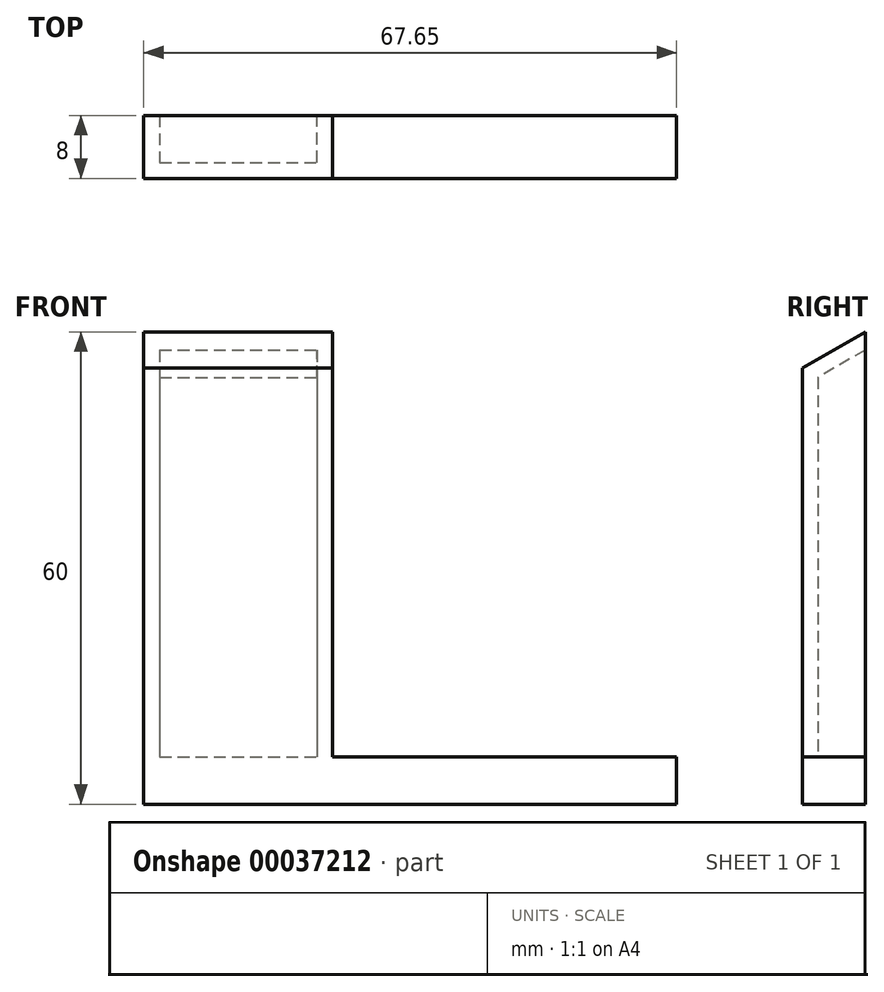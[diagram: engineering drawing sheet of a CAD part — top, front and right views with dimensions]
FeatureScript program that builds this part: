
annotation { "Feature Type Name" : "Feature", "Feature Type Description" : "" }
export const myFeature = defineFeature(function(context is Context, id is Id, definition is map)
    precondition{}
    {
        {
            var Q0;
            Q0=qCreatedBy(makeId("Front.planeOp"),FACE);
            var sketch = newSketch(context, id + "F0", { "sketchPlane" : qUnion([Q0])});
            skLineSegment(sketch, "E0.rect.bottom", {"start": v(-12, 27) * mm, "end": v(12, 27) * mm, "construction": true});
            skLineSegment(sketch, "E0.rect.top", {"start": v(-12, -27) * mm, "end": v(12, -27) * mm, "construction": true});
            skLineSegment(sketch, "E0.rect.left", {"start": v(-12, 27) * mm, "end": v(-12, -27) * mm, "construction": true});
            skLineSegment(sketch, "E0.rect.right", {"start": v(12, 27) * mm, "end": v(12, -27) * mm, "construction": true});
            skPoint(sketch, "E0.rect.middle", {"position": v(0, 0) * mm});
            skLineSegment(sketch, "E1.rect.bottom", {"start": v(-12, 27) * mm, "end": v(12, 27) * mm});
            skLineSegment(sketch, "E1.rect.top", {"start": v(-12, -27) * mm, "end": v(12, -27) * mm});
            skLineSegment(sketch, "E1.rect.left", {"start": v(-12, 27) * mm, "end": v(-12, -27) * mm});
            skLineSegment(sketch, "E1.rect.right", {"start": v(12, 27) * mm, "end": v(12, -27) * mm});
            skLineSegment(sketch, "E2.rect.bottom", {"start": v(-10, 25) * mm, "end": v(10, 25) * mm});
            skLineSegment(sketch, "E2.rect.top", {"start": v(-10, -25) * mm, "end": v(10, -25) * mm});
            skLineSegment(sketch, "E2.rect.left", {"start": v(-10, 25) * mm, "end": v(-10, -25) * mm});
            skLineSegment(sketch, "E2.rect.right", {"start": v(10, 25) * mm, "end": v(10, -25) * mm});
            skLineSegment(sketch, "E3", {"start": v(-10, -25) * mm, "end": v(-10, -27) * mm});
            skLineSegment(sketch, "E4", {"start": v(10, -25) * mm, "end": v(10, -27) * mm});
            skSolve(sketch);
        }
        {
            var Q0;
            Q0=makeQuery(id+"F0.imprint","IMPRINT",FACE,{"disambiguationData":[TD([[makeQuery(id+"F0.imprint","IMPRINT",EDGE,{"derivedFrom":sQuery(id+"F0.wireOp",EDGE,"E1.rect.bottom")}),-1.0]])]});
            var Q1;
            Q1=makeQuery(id+"F0.imprint","IMPRINT",FACE,{"disambiguationData":[TD([[makeQuery(id+"F0.imprint","IMPRINT",EDGE,{"derivedFrom":sQuery(id+"F0.wireOp",EDGE,"E2.rect.bottom")}),-1.0]])]});
            var Q2;
            Q2=makeQuery(id+"F0.imprint","IMPRINT",FACE,{"disambiguationData":[TD([[makeQuery(id+"F0.imprint","IMPRINT",EDGE,{"derivedFrom":sQuery(id+"F0.wireOp",EDGE,"E2.rect.top")}),-1.0]])]});
            extrude(context, id + "F1", {"entities" : qUnion([Q0, Q1, Q2]), "depth" : 8 * mm});
        }
        {
            var Q0;
            Q0=qCreatedBy(makeId("Right.planeOp"),FACE);
            var sketch = newSketch(context, id + "F2", { "sketchPlane" : qUnion([Q0])});
            skLineSegment(sketch, "E5", {"start": v(0, -22.38) * mm, "end": v(-8, -27) * mm});
            skLineSegment(sketch, "E6", {"start": v(0, -22.38) * mm, "end": v(0, -27) * mm});
            skLineSegment(sketch, "E7", {"start": v(0, -27) * mm, "end": v(-8, -27) * mm});
            skLineSegment(sketch, "E8", {"start": v(0, 27) * mm, "end": v(-8, 22.38) * mm});
            skLineSegment(sketch, "E9", {"start": v(-8, 22.38) * mm, "end": v(-8, 27) * mm});
            skLineSegment(sketch, "E10", {"start": v(-8, 27) * mm, "end": v(0, 27) * mm});
            skLineSegment(sketch, "E11", {"start": v(-6.5, -26.13) * mm, "end": v(-8, -26.13) * mm, "construction": true});
            skLineSegment(sketch, "E12", {"start": v(-6.5, -24.13) * mm, "end": v(-1.5, -21.25) * mm});
            skLineSegment(sketch, "E13", {"start": v(-6.5, 21.25) * mm, "end": v(-1.5, 24.13) * mm});
            skLineSegment(sketch, "E14", {"start": v(-6.5, -24.13) * mm, "end": v(-6.5, 21.25) * mm});
            skLineSegment(sketch, "E15", {"start": v(-1.5, 24.13) * mm, "end": v(-1.5, -21.25) * mm});
            skLineSegment(sketch, "E16", {"start": v(-6.5, -24.13) * mm, "end": v(-6.5, -26.13) * mm});
            skLineSegment(sketch, "E17", {"start": v(-1.5, -21.25) * mm, "end": v(-1.5, -23.25) * mm});
            skLineSegment(sketch, "E18", {"start": v(-6.5, 21.25) * mm, "end": v(-6.5, 23.25) * mm});
            skLineSegment(sketch, "E19", {"start": v(-1.5, 24.13) * mm, "end": v(-1.5, 26.13) * mm});
            skLineSegment(sketch, "E20", {"start": v(-8, 22.38) * mm, "end": v(-6.5, 22.38) * mm});
            skLineSegment(sketch, "E21", {"start": v(-1.5, 26.13) * mm, "end": v(0, 26.13) * mm});
            skLineSegment(sketch, "E22", {"start": v(0, -22.38) * mm, "end": v(-1.5, -22.38) * mm, "construction": true});
            skLineSegment(sketch, "E23", {"start": v(-1.5, 24.13) * mm, "end": v(0, 25) * mm});
            skLineSegment(sketch, "E24", {"start": v(0, 25) * mm, "end": v(0.8, 25.47) * mm});
            skLineSegment(sketch, "E25", {"start": v(0, -22.38) * mm, "end": v(0.8, -21.91) * mm});
            skLineSegment(sketch, "E26", {"start": v(0.8, -21.91) * mm, "end": v(0.8, 25.47) * mm});
            skLineSegment(sketch, "E27", {"start": v(-1.5, -21.25) * mm, "end": v(0.8, -19.91) * mm});
            skLineSegment(sketch, "E28", {"start": v(-6.5, -24.13) * mm, "end": v(-8.13, -25.08) * mm});
            skLineSegment(sketch, "E29", {"start": v(-8.13, -25.08) * mm, "end": v(-8, -27) * mm});
            skLineSegment(sketch, "E30", {"start": v(0.8, -20.24) * mm, "end": v(-8.1, -25.39) * mm});
            skSolve(sketch);
        }
        {
            var Q0;
            {var subQ1=sQuery(id+"F2.wireOp",EDGE,"E9");Q0=makeQuery(id+"F2.imprint","IMPRINT",FACE,{"disambiguationData":[TD([[makeQuery(id+"F2.imprint","IMPRINT",EDGE,{"derivedFrom":subQ1}),-1.0]])]});}
            extrude(context, id + "F3", {"entities" : qUnion([Q0]), "operationType" : NewBodyOperationType.REMOVE, "oppositeDirection" : true, "depth" : 50 * mm});
        }
        {
            var Q0;
            {var subQ1=sQuery(id+"F2.wireOp",EDGE,"E9");Q0=makeQuery(id+"F2.imprint","IMPRINT",FACE,{"disambiguationData":[TD([[makeQuery(id+"F2.imprint","IMPRINT",EDGE,{"derivedFrom":subQ1}),-1.0]])]});}
            extrude(context, id + "F4", {"entities" : qUnion([Q0]), "operationType" : NewBodyOperationType.REMOVE, "depth" : 25.4 * mm});
        }
        {
            var Q0;
            Q0=makeQuery(id+"F1.opExtrude","CAP_FACE",FACE,{"disambiguationData":[OSD([sQuery(id+"F0.wireOp",EDGE,"E1.rect.bottom"),sQuery(id+"F0.wireOp",EDGE,"E1.rect.top"),sQuery(id+"F0.wireOp",EDGE,"E1.rect.left"),sQuery(id+"F0.wireOp",EDGE,"E1.rect.right")])],"isStart":true});
            var Q1;
            Q1=makeQuery(id+"F1.opExtrude","SWEPT_FACE",FACE,{"disambiguationData":[OSD([sQuery(id+"F0.wireOp",EDGE,"E1.rect.top")])]});
            shell(context, id + "F5", {"entities" : qUnion([Q0, Q1]), "thickness" : 2 * mm});
        }
        {
            var Q0;
            Q0=makeQuery(id+"F1.opExtrude","CAP_FACE",FACE,{"disambiguationData":[OSD([sQuery(id+"F0.wireOp",EDGE,"E1.rect.bottom"),sQuery(id+"F0.wireOp",EDGE,"E1.rect.top"),sQuery(id+"F0.wireOp",EDGE,"E1.rect.left"),sQuery(id+"F0.wireOp",EDGE,"E1.rect.right")])],"isStart":true});
            var sketch = newSketch(context, id + "F6", { "sketchPlane" : qUnion([Q0])});
            skLineSegment(sketch, "E31", {"start": v(12, -27) * mm, "end": v(12, -33) * mm});
            skLineSegment(sketch, "E32", {"start": v(12, -33) * mm, "end": v(-55.65, -33) * mm});
            skLineSegment(sketch, "E33", {"start": v(-12, -27) * mm, "end": v(-55.65, -27) * mm});
            skLineSegment(sketch, "E34", {"start": v(10, -27) * mm, "end": v(10, -33) * mm});
            skLineSegment(sketch, "E35", {"start": v(-55.65, -33) * mm, "end": v(-55.65, -27) * mm});
            skLineSegment(sketch, "E36", {"start": v(12, -31) * mm, "end": v(-55.65, -31) * mm});
            skLineSegment(sketch, "E37", {"start": v(-12, -27) * mm, "end": v(-10, -27) * mm});
            skLineSegment(sketch, "E38", {"start": v(-10, -27) * mm, "end": v(10, -27) * mm});
            skLineSegment(sketch, "E39", {"start": v(-10, -27) * mm, "end": v(-10, -29) * mm});
            skLineSegment(sketch, "E40", {"start": v(-10, -29) * mm, "end": v(-55.65, -29) * mm});
            skLineSegment(sketch, "E41", {"start": v(-53.65, -27) * mm, "end": v(-53.65, -33) * mm});
            skLineSegment(sketch, "E42", {"start": v(-10, -31) * mm, "end": v(-10, -33) * mm});
            skSolve(sketch);
        }
        {
            var Q0;
            {var subQ0=makeQuery(id+"F1.opExtrude","CAP_EDGE",EDGE,{"disambiguationData":[OSD([sQuery(id+"F0.wireOp",EDGE,"E1.rect.top")])],"isStart":true});Q0=makeQuery(id+"F6.imprint","IMPRINT",FACE,{"disambiguationData":[TD([[makeQuery(id+"F6.imprint","IMPRINT",EDGE,{"derivedFrom":subQ0}),1.0]])]});}
            var Q1;
            {var subQ3=sQuery(id+"F6.wireOp",EDGE,"E31");var subQ5=sQuery(id+"F6.wireOp",EDGE,"E32");var subQ7=makeQuery(id+"F6.imprint","INTERSECT",VERTEX,{"derivedFrom":[subQ3,subQ5]});Q1=makeQuery(id+"F6.imprint","IMPRINT",FACE,{"disambiguationData":[TD([[makeQuery(id+"F6.imprint","IMPRINT",EDGE,{"disambiguationData":[TD([[subQ7,1.0]])],"derivedFrom":subQ3}),-1.0]])]});}
            var Q2;
            {var subQ0=sQuery(id+"F6.wireOp",EDGE,"E42");Q2=makeQuery(id+"F6.imprint","IMPRINT",FACE,{"disambiguationData":[TD([[makeQuery(id+"F6.imprint","IMPRINT",EDGE,{"derivedFrom":subQ0}),1.0]])]});}
            var Q3;
            {var subQ0=sQuery(id+"F6.wireOp",EDGE,"E42");Q3=makeQuery(id+"F6.imprint","IMPRINT",FACE,{"disambiguationData":[TD([[makeQuery(id+"F6.imprint","IMPRINT",EDGE,{"derivedFrom":subQ0}),-1.0]])]});}
            var Q4;
            {var subQ6=sQuery(id+"F6.wireOp",EDGE,"E37");Q4=makeQuery(id+"F6.imprint","IMPRINT",FACE,{"disambiguationData":[TD([[makeQuery(id+"F6.imprint","IMPRINT",EDGE,{"derivedFrom":subQ6}),1.0]])]});}
            var Q5;
            {var subQ3=sQuery(id+"F6.wireOp",EDGE,"E33");var subQ5=sQuery(id+"F6.wireOp",EDGE,"E35");var subQ7=makeQuery(id+"F6.imprint","INTERSECT",VERTEX,{"derivedFrom":[subQ3,subQ5]});Q5=makeQuery(id+"F6.imprint","IMPRINT",FACE,{"disambiguationData":[TD([[makeQuery(id+"F6.imprint","IMPRINT",EDGE,{"disambiguationData":[TD([[subQ7,1.0]])],"derivedFrom":subQ3}),1.0]])]});}
            var Q6;
            {var subQ3=sQuery(id+"F6.wireOp",EDGE,"E35");var subQ5=sQuery(id+"F6.wireOp",EDGE,"E36");var subQ7=makeQuery(id+"F6.imprint","INTERSECT",VERTEX,{"derivedFrom":[subQ3,subQ5]});Q6=makeQuery(id+"F6.imprint","IMPRINT",FACE,{"disambiguationData":[TD([[makeQuery(id+"F6.imprint","IMPRINT",EDGE,{"disambiguationData":[TD([[subQ7,-1.0]])],"derivedFrom":subQ3}),-1.0]])]});}
            var Q7;
            {var subQ3=sQuery(id+"F6.wireOp",EDGE,"E32");var subQ5=sQuery(id+"F6.wireOp",EDGE,"E35");var subQ7=makeQuery(id+"F6.imprint","INTERSECT",VERTEX,{"derivedFrom":[subQ3,subQ5]});Q7=makeQuery(id+"F6.imprint","IMPRINT",FACE,{"disambiguationData":[TD([[makeQuery(id+"F6.imprint","IMPRINT",EDGE,{"disambiguationData":[TD([[subQ7,1.0]])],"derivedFrom":subQ3}),-1.0]])]});}
            var Q8;
            {var subQ6=sQuery(id+"F6.wireOp",EDGE,"E38");Q8=makeQuery(id+"F6.imprint","IMPRINT",FACE,{"disambiguationData":[TD([[makeQuery(id+"F6.imprint","IMPRINT",EDGE,{"derivedFrom":subQ6}),-1.0]])]});}
            extrude(context, id + "F7", {"entities" : qUnion([Q0, Q1, Q2, Q3, Q4, Q5, Q6, Q7, Q8]), "operationType" : NewBodyOperationType.ADD, "oppositeDirection" : true, "depth" : 8 * mm});
        }
    });
